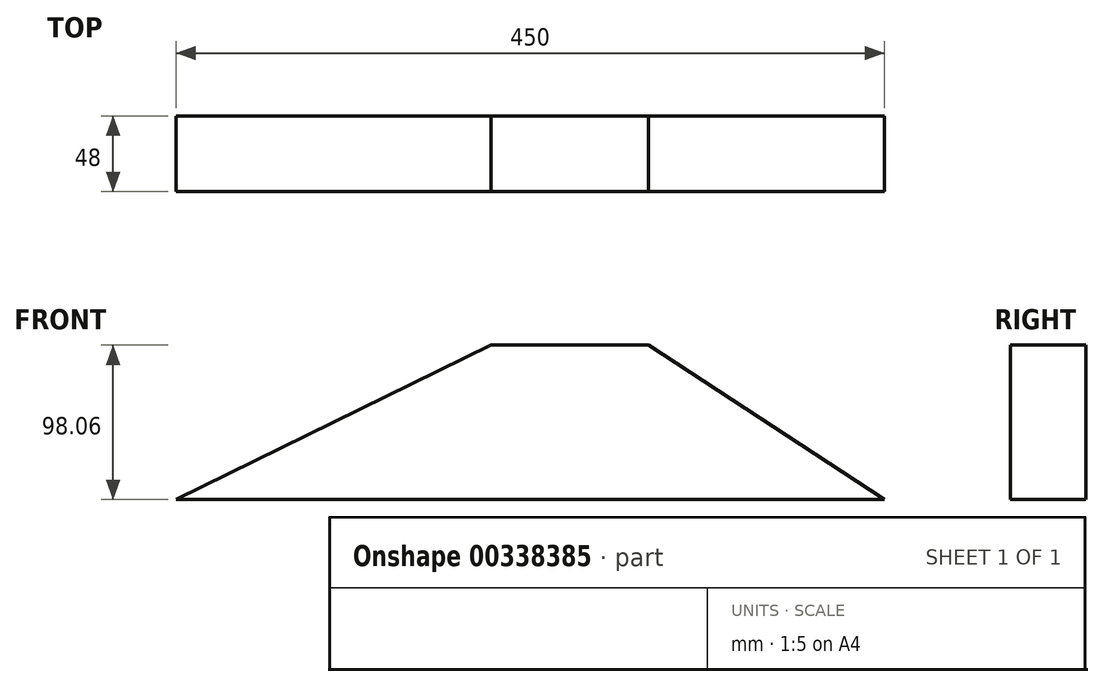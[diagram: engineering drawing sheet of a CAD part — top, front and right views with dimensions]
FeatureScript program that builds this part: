
annotation { "Feature Type Name" : "Feature", "Feature Type Description" : "" }
export const myFeature = defineFeature(function(context is Context, id is Id, definition is map)
    precondition{}
    {
        {
            var Q0;
            Q0=qCreatedBy(makeId("Front.planeOp"),FACE);
            var sketch = newSketch(context, id + "F0", { "sketchPlane" : qUnion([Q0])});
            skLineSegment(sketch, "E0.bottom", {"start": v(50, -49) * mm, "end": v(-50, -49) * mm});
            skLineSegment(sketch, "E0.top", {"start": v(50, 49) * mm, "end": v(-50, 49) * mm});
            skLineSegment(sketch, "E0.left", {"start": v(50, -49) * mm, "end": v(50, 49) * mm});
            skLineSegment(sketch, "E0.right", {"start": v(-50, -49) * mm, "end": v(-50, 49) * mm});
            skPoint(sketch, "E0.middle", {"position": v(0, 0) * mm});
            skLineSegment(sketch, "E1.bottom", {"start": v(50, -49) * mm, "end": v(200, -49) * mm});
            skLineSegment(sketch, "E1.left", {"start": v(50, -49) * mm, "end": v(50, 49.06) * mm});
            skLineSegment(sketch, "E2", {"start": v(200, -49) * mm, "end": v(50, 49.06) * mm});
            skLineSegment(sketch, "E3.bottom", {"start": v(-50, -49) * mm, "end": v(-250, -49) * mm});
            skLineSegment(sketch, "E3.left", {"start": v(-50, -49) * mm, "end": v(-50, 49.06) * mm});
            skLineSegment(sketch, "E4", {"start": v(-50, 49.06) * mm, "end": v(-250, -49) * mm});
            skSolve(sketch);
        }
        {
            var Q0;
            Q0=makeQuery(id+"F0.imprint","IMPRINT",FACE,{"disambiguationData":[TD([[makeQuery(id+"F0.imprint","IMPRINT",EDGE,{"derivedFrom":sQuery(id+"F0.wireOp",EDGE,"7h4oqL3a-DEVb-f7Zc-LBDy-PHsN7Ko9ZoFB.bottom")}),1.0]])]});
            var Q1;
            Q1=makeQuery(id+"F0.imprint","IMPRINT",FACE,{"disambiguationData":[TD([[makeQuery(id+"F0.imprint","IMPRINT",EDGE,{"derivedFrom":sQuery(id+"F0.wireOp",EDGE,"BjaezAv7-3NPQ-lNIr-wQXZ-BZ2Sa1eiwDw3.top")}),1.0]])]});
            var Q2;
            Q2=makeQuery(id+"F0.imprint","IMPRINT",FACE,{"disambiguationData":[TD([[makeQuery(id+"F0.imprint","IMPRINT",EDGE,{"derivedFrom":sQuery(id+"F0.wireOp",EDGE,"Ls5YBP2p-ygmQ-LDJd-DizF-RlDbNUUytozA.bottom")}),1.0]])]});
            var Q3;
            Q3=makeQuery(id+"F0.imprint","IMPRINT",FACE,{"disambiguationData":[TD([[makeQuery(id+"F0.imprint","IMPRINT",EDGE,{"derivedFrom":sQuery(id+"F0.wireOp",EDGE,"7g4hM47W-e6Kj-Eb7D-l9s5-i8vfCJIvhB6S.bottom")}),1.0]])]});
            var Q4;
            Q4=makeQuery(id+"F0.imprint","IMPRINT",FACE,{"disambiguationData":[TD([[makeQuery(id+"F0.imprint","IMPRINT",EDGE,{"derivedFrom":sQuery(id+"F0.wireOp",EDGE,"YNs8NOTm-8gwP-Qp2Z-9UJN-R3UGSaFyRMmN.bottom")}),-1.0]])]});
            var Q5;
            {var subQ0=sQuery(id+"F0.wireOp",EDGE,"E0.bottom");Q5=makeQuery(id+"F0.imprint","IMPRINT",FACE,{"disambiguationData":[TD([[makeQuery(id+"F0.imprint","IMPRINT",EDGE,{"derivedFrom":subQ0}),-1.0]])]});}
            var Q6;
            {var subQ0=sQuery(id+"F0.wireOp",EDGE,"E3.bottom");Q6=makeQuery(id+"F0.imprint","IMPRINT",FACE,{"disambiguationData":[TD([[makeQuery(id+"F0.imprint","IMPRINT",EDGE,{"derivedFrom":subQ0}),-1.0]])]});}
            var Q7;
            {var subQ0=sQuery(id+"F0.wireOp",EDGE,"E1.bottom");Q7=makeQuery(id+"F0.imprint","IMPRINT",FACE,{"disambiguationData":[TD([[makeQuery(id+"F0.imprint","IMPRINT",EDGE,{"derivedFrom":subQ0}),1.0]])]});}
            extrude(context, id + "F1", {"entities" : qUnion([Q0, Q1, Q2, Q3, Q4, Q5, Q6, Q7]), "depth" : 48 * mm});
        }
    });
